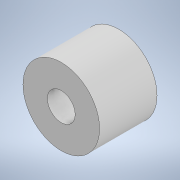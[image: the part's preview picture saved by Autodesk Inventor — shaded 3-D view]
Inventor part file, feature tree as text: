
AUTODESK INVENTOR PART (.ipt)
format: ipt  version: 2021 (Build 250183000, 183)  size: 96,256 bytes
history: native  units: mm
features: extrude x1, sketch x1
ambient origin geometry x8: Origin, YZ Plane, XZ Plane, XY Plane, X Axis, Y Axis, Z Axis, Center Point
bodies: Solid1 (feature_tree)
feature tree (2):
  extrude  "Extrusion1"  Depth=6.0mm
  sketch  "Sketch1"  dims[d0=2.9mm d1=8.0mm d2=6.0mm d3=0.0mm]
